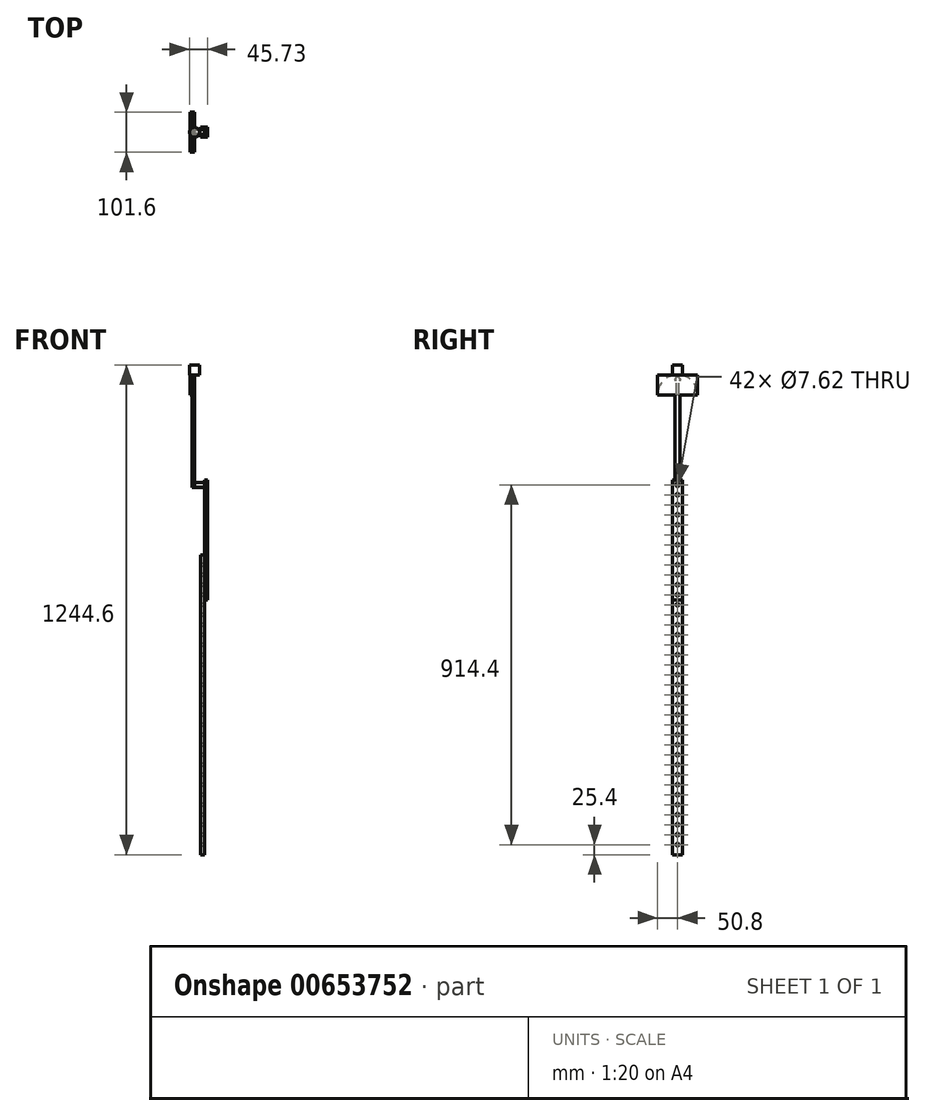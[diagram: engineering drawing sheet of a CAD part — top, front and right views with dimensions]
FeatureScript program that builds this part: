
annotation { "Feature Type Name" : "Feature", "Feature Type Description" : "" }
export const myFeature = defineFeature(function(context is Context, id is Id, definition is map)
    precondition{}
    {
        {
            var Q0;
            Q0=qCreatedBy(makeId("Right.planeOp"),FACE);
            var sketch = newSketch(context, id + "F0", { "sketchPlane" : qUnion([Q0])});
            skLineSegment(sketch, "E0.bottom", {"start": v(0, 762) * mm, "end": v(25.4, 762) * mm});
            skLineSegment(sketch, "E0.top", {"start": v(0, 0) * mm, "end": v(25.4, 0) * mm});
            skLineSegment(sketch, "E0.left", {"start": v(0, 762) * mm, "end": v(0, 0) * mm});
            skLineSegment(sketch, "E0.right", {"start": v(25.4, 762) * mm, "end": v(25.4, 0) * mm});
            skCircle(sketch, "E1", {"center": v(12.7, 25.4) * mm, "radius": 3.81 * mm});
            skCircle(sketch, "E2.0.1.0", {"center": v(12.7, 50.8) * mm, "radius": 3.81 * mm});
            skCircle(sketch, "E2.0.2.0", {"center": v(12.7, 76.2) * mm, "radius": 3.81 * mm});
            skCircle(sketch, "E2.0.3.0", {"center": v(12.7, 101.6) * mm, "radius": 3.81 * mm});
            skCircle(sketch, "E2.0.4.0", {"center": v(12.7, 127) * mm, "radius": 3.81 * mm});
            skCircle(sketch, "E2.0.5.0", {"center": v(12.7, 152.4) * mm, "radius": 3.81 * mm});
            skCircle(sketch, "E2.0.6.0", {"center": v(12.7, 177.8) * mm, "radius": 3.81 * mm});
            skCircle(sketch, "E2.0.7.0", {"center": v(12.7, 203.2) * mm, "radius": 3.81 * mm});
            skCircle(sketch, "E2.0.8.0", {"center": v(12.7, 228.6) * mm, "radius": 3.81 * mm});
            skCircle(sketch, "E2.0.9.0", {"center": v(12.7, 254) * mm, "radius": 3.81 * mm});
            skCircle(sketch, "E2.0.10.0", {"center": v(12.7, 279.4) * mm, "radius": 3.81 * mm});
            skCircle(sketch, "E2.0.11.0", {"center": v(12.7, 304.8) * mm, "radius": 3.81 * mm});
            skCircle(sketch, "E2.0.12.0", {"center": v(12.7, 330.2) * mm, "radius": 3.81 * mm});
            skCircle(sketch, "E2.0.13.0", {"center": v(12.7, 355.6) * mm, "radius": 3.81 * mm});
            skCircle(sketch, "E2.0.14.0", {"center": v(12.7, 381) * mm, "radius": 3.81 * mm});
            skCircle(sketch, "E2.0.15.0", {"center": v(12.7, 406.4) * mm, "radius": 3.81 * mm});
            skCircle(sketch, "E2.0.16.0", {"center": v(12.7, 431.8) * mm, "radius": 3.81 * mm});
            skCircle(sketch, "E2.0.17.0", {"center": v(12.7, 457.2) * mm, "radius": 3.81 * mm});
            skCircle(sketch, "E2.0.18.0", {"center": v(12.7, 482.6) * mm, "radius": 3.81 * mm});
            skCircle(sketch, "E2.0.19.0", {"center": v(12.7, 508) * mm, "radius": 3.81 * mm});
            skCircle(sketch, "E2.0.20.0", {"center": v(12.7, 533.4) * mm, "radius": 3.81 * mm});
            skCircle(sketch, "E2.0.21.0", {"center": v(12.7, 558.8) * mm, "radius": 3.81 * mm});
            skCircle(sketch, "E2.0.22.0", {"center": v(12.7, 584.2) * mm, "radius": 3.81 * mm});
            skCircle(sketch, "E2.0.23.0", {"center": v(12.7, 609.6) * mm, "radius": 3.81 * mm});
            skCircle(sketch, "E2.0.24.0", {"center": v(12.7, 635) * mm, "radius": 3.81 * mm});
            skCircle(sketch, "E2.0.25.0", {"center": v(12.7, 660.4) * mm, "radius": 3.81 * mm});
            skCircle(sketch, "E2.0.26.0", {"center": v(12.7, 685.8) * mm, "radius": 3.81 * mm});
            skCircle(sketch, "E2.0.27.0", {"center": v(12.7, 711.2) * mm, "radius": 3.81 * mm});
            skCircle(sketch, "E2.0.28.0", {"center": v(12.7, 736.6) * mm, "radius": 3.81 * mm});
            skLineSegment(sketch, "E2.direction1", {"start": v(12.7, 25.4) * mm, "end": v(38.1, 25.4) * mm, "construction": true});
            skLineSegment(sketch, "E2.direction2", {"start": v(12.7, 25.4) * mm, "end": v(12.7, 50.8) * mm, "construction": true});
            skSolve(sketch);
        }
        {
            var Q0;
            Q0=makeQuery(id+"F0.imprint","IMPRINT",FACE,{"disambiguationData":[TD([[makeQuery(id+"F0.imprint","IMPRINT",EDGE,{"derivedFrom":sQuery(id+"F0.wireOp",EDGE,"E0.bottom")}),-1.0]])]});
            extrude(context, id + "F1", {"entities" : qUnion([Q0]), "depth" : 9.52 * mm, "offsetDistance" : 25.4 * mm});
        }
        {
            var Q0;
            Q0=makeQuery(id+"F1.opExtrude","CAP_FACE",FACE,{"disambiguationData":[OSD([sQuery(id+"F0.wireOp",EDGE,"E0.bottom"),sQuery(id+"F0.wireOp",EDGE,"E0.top"),sQuery(id+"F0.wireOp",EDGE,"E0.left"),sQuery(id+"F0.wireOp",EDGE,"E0.right"),sQuery(id+"F0.wireOp",EDGE,"E1"),sQuery(id+"F0.wireOp",EDGE,"E2.0.1.0"),sQuery(id+"F0.wireOp",EDGE,"E2.0.2.0"),sQuery(id+"F0.wireOp",EDGE,"E2.0.3.0"),sQuery(id+"F0.wireOp",EDGE,"E2.0.4.0"),sQuery(id+"F0.wireOp",EDGE,"E2.0.5.0"),sQuery(id+"F0.wireOp",EDGE,"E2.0.6.0"),sQuery(id+"F0.wireOp",EDGE,"E2.0.7.0"),sQuery(id+"F0.wireOp",EDGE,"E2.0.8.0"),sQuery(id+"F0.wireOp",EDGE,"E2.0.9.0"),sQuery(id+"F0.wireOp",EDGE,"E2.0.10.0"),sQuery(id+"F0.wireOp",EDGE,"E2.0.11.0"),sQuery(id+"F0.wireOp",EDGE,"E2.0.12.0"),sQuery(id+"F0.wireOp",EDGE,"E2.0.13.0"),sQuery(id+"F0.wireOp",EDGE,"E2.0.14.0"),sQuery(id+"F0.wireOp",EDGE,"E2.0.15.0"),sQuery(id+"F0.wireOp",EDGE,"E2.0.16.0"),sQuery(id+"F0.wireOp",EDGE,"E2.0.17.0"),sQuery(id+"F0.wireOp",EDGE,"E2.0.18.0"),sQuery(id+"F0.wireOp",EDGE,"E2.0.19.0"),sQuery(id+"F0.wireOp",EDGE,"E2.0.20.0"),sQuery(id+"F0.wireOp",EDGE,"E2.0.21.0"),sQuery(id+"F0.wireOp",EDGE,"E2.0.22.0"),sQuery(id+"F0.wireOp",EDGE,"E2.0.23.0"),sQuery(id+"F0.wireOp",EDGE,"E2.0.24.0"),sQuery(id+"F0.wireOp",EDGE,"E2.0.25.0"),sQuery(id+"F0.wireOp",EDGE,"E2.0.26.0"),sQuery(id+"F0.wireOp",EDGE,"E2.0.27.0"),sQuery(id+"F0.wireOp",EDGE,"E2.0.28.0")])],"isStart":false});
            var sketch = newSketch(context, id + "F2", { "sketchPlane" : qUnion([Q0])});
            skLineSegment(sketch, "E3.bottom", {"start": v(0, 952.5) * mm, "end": v(25.4, 952.5) * mm});
            skLineSegment(sketch, "E3.top", {"start": v(0, 647.7) * mm, "end": v(25.4, 647.7) * mm});
            skLineSegment(sketch, "E3.left", {"start": v(0, 952.5) * mm, "end": v(0, 647.7) * mm});
            skLineSegment(sketch, "E3.right", {"start": v(25.4, 952.5) * mm, "end": v(25.4, 647.7) * mm});
            skPoint(sketch, "E4", {"position": v(12.7, 25.4) * mm});
            skCircle(sketch, "E5", {"center": v(12.7, 660.4) * mm, "radius": 3.81 * mm});
            skCircle(sketch, "E6.0.1.0", {"center": v(12.7, 685.8) * mm, "radius": 3.81 * mm});
            skCircle(sketch, "E6.0.2.0", {"center": v(12.7, 711.2) * mm, "radius": 3.81 * mm});
            skCircle(sketch, "E6.0.3.0", {"center": v(12.7, 736.6) * mm, "radius": 3.81 * mm});
            skCircle(sketch, "E6.0.4.0", {"center": v(12.7, 762) * mm, "radius": 3.81 * mm});
            skCircle(sketch, "E6.0.5.0", {"center": v(12.7, 787.4) * mm, "radius": 3.81 * mm});
            skCircle(sketch, "E6.0.6.0", {"center": v(12.7, 812.8) * mm, "radius": 3.81 * mm});
            skCircle(sketch, "E6.0.7.0", {"center": v(12.7, 838.2) * mm, "radius": 3.81 * mm});
            skCircle(sketch, "E6.0.8.0", {"center": v(12.7, 863.6) * mm, "radius": 3.81 * mm});
            skCircle(sketch, "E6.0.9.0", {"center": v(12.7, 889) * mm, "radius": 3.81 * mm});
            skCircle(sketch, "E6.0.10.0", {"center": v(12.7, 914.4) * mm, "radius": 3.81 * mm});
            skCircle(sketch, "E6.0.11.0", {"center": v(12.7, 939.8) * mm, "radius": 3.81 * mm});
            skLineSegment(sketch, "E6.direction1", {"start": v(12.7, 660.4) * mm, "end": v(38.1, 660.4) * mm, "construction": true});
            skLineSegment(sketch, "E6.direction2", {"start": v(12.7, 660.4) * mm, "end": v(12.7, 685.8) * mm, "construction": true});
            skSolve(sketch);
        }
        {
            var Q0;
            {var subQ0=sQuery(id+"F2.wireOp",EDGE,"E3.bottom");Q0=makeQuery(id+"F2.imprint","IMPRINT",FACE,{"disambiguationData":[TD([[makeQuery(id+"F2.imprint","IMPRINT",EDGE,{"derivedFrom":subQ0}),-1.0]])]});}
            var Q1;
            {var subQ3=sQuery(id+"F2.wireOp",EDGE,"E3.top");Q1=makeQuery(id+"F2.imprint","IMPRINT",FACE,{"disambiguationData":[TD([[makeQuery(id+"F2.imprint","IMPRINT",EDGE,{"derivedFrom":subQ3}),1.0]])]});}
            extrude(context, id + "F3", {"entities" : qUnion([Q0, Q1]), "depth" : 7.62 * mm, "offsetDistance" : 25.4 * mm});
        }
        {
            var Q0;
            Q0=makeQuery(id+"F3.opExtrude","CAP_FACE",FACE,{"disambiguationData":[OSD([sQuery(id+"F2.wireOp",EDGE,"E3.bottom"),sQuery(id+"F2.wireOp",EDGE,"E3.top"),sQuery(id+"F2.wireOp",EDGE,"E3.left"),sQuery(id+"F2.wireOp",EDGE,"E3.right"),sQuery(id+"F2.wireOp",EDGE,"E5"),sQuery(id+"F2.wireOp",EDGE,"E6.0.1.0"),sQuery(id+"F2.wireOp",EDGE,"E6.0.2.0"),sQuery(id+"F2.wireOp",EDGE,"E6.0.3.0"),sQuery(id+"F2.wireOp",EDGE,"E6.0.4.0"),sQuery(id+"F2.wireOp",EDGE,"E6.0.5.0"),sQuery(id+"F2.wireOp",EDGE,"E6.0.6.0"),sQuery(id+"F2.wireOp",EDGE,"E6.0.7.0"),sQuery(id+"F2.wireOp",EDGE,"E6.0.8.0"),sQuery(id+"F2.wireOp",EDGE,"E6.0.9.0"),sQuery(id+"F2.wireOp",EDGE,"E6.0.10.0"),sQuery(id+"F2.wireOp",EDGE,"E6.0.11.0")])],"isStart":true});
            var sketch = newSketch(context, id + "F4", { "sketchPlane" : qUnion([Q0])});
            skCircle(sketch, "E7", {"center": v(-12.7, 939.8) * mm, "radius": 6.35 * mm});
            skSolve(sketch);
        }
        {
            var Q0;
            Q0=makeQuery(id+"F4.imprint","IMPRINT",FACE,{"disambiguationData":[TD([[makeQuery(id+"F4.imprint","IMPRINT",EDGE,{"derivedFrom":sQuery(id+"F4.wireOp",EDGE,"E7")}),1.0]])]});
            extrude(context, id + "F5", {"entities" : qUnion([Q0]), "operationType" : NewBodyOperationType.ADD, "depth" : 25.4 * mm, "offsetDistance" : 25.4 * mm});
        }
        {
            var Q0;
            Q0=makeQuery(id+"F5.opExtrude","CAP_FACE",FACE,{"disambiguationData":[OSD([sQuery(id+"F2.wireOp",EDGE,"E6.0.11.0"),sQuery(id+"F4.wireOp",EDGE,"E7")])],"isStart":false});
            var sketch = newSketch(context, id + "F6", { "sketchPlane" : qUnion([Q0])});
            skLineSegment(sketch, "E8.bottom", {"start": v(-19.05, 1193.8) * mm, "end": v(-6.35, 1193.8) * mm});
            skLineSegment(sketch, "E8.top", {"start": v(-19.05, 933.45) * mm, "end": v(-6.35, 933.45) * mm});
            skLineSegment(sketch, "E8.left", {"start": v(-19.05, 1193.8) * mm, "end": v(-19.05, 933.45) * mm});
            skLineSegment(sketch, "E8.right", {"start": v(-6.35, 1193.8) * mm, "end": v(-6.35, 933.45) * mm});
            skPoint(sketch, "E9", {"position": v(-12.7, 939.8) * mm});
            skLineSegment(sketch, "E10.bottom", {"start": v(-63.5, 1168.4) * mm, "end": v(38.1, 1168.4) * mm});
            skLineSegment(sketch, "E10.top", {"start": v(-63.5, 1219.2) * mm, "end": v(38.1, 1219.2) * mm});
            skLineSegment(sketch, "E10.left", {"start": v(-63.5, 1168.4) * mm, "end": v(-63.5, 1219.2) * mm});
            skLineSegment(sketch, "E10.right", {"start": v(38.1, 1168.4) * mm, "end": v(38.1, 1219.2) * mm});
            skSolve(sketch);
        }
        {
            var Q0;
            Q0=makeQuery(id+"F6.imprint","IMPRINT",FACE,{"disambiguationData":[TD([[makeQuery(id+"F6.imprint","IMPRINT",EDGE,{"derivedFrom":makeQuery(id+"F5.opExtrude","CAP_EDGE",EDGE,{"disambiguationData":[OSD([sQuery(id+"F2.wireOp",EDGE,"E6.0.11.0")])],"isStart":false})}),1.0]])]});
            var Q1;
            {var subQ5=sQuery(id+"F6.wireOp",EDGE,"E8.bottom");Q1=makeQuery(id+"F6.imprint","IMPRINT",FACE,{"disambiguationData":[TD([[makeQuery(id+"F6.imprint","IMPRINT",EDGE,{"derivedFrom":subQ5}),1.0]])]});}
            var Q2;
            {var subQ0=sQuery(id+"F6.wireOp",EDGE,"E8.bottom");Q2=makeQuery(id+"F6.imprint","IMPRINT",FACE,{"disambiguationData":[TD([[makeQuery(id+"F6.imprint","IMPRINT",EDGE,{"derivedFrom":subQ0}),-1.0]])]});}
            var Q3;
            {var subQ0=sQuery(id+"F6.wireOp",EDGE,"E10.bottom");var subQ1=sQuery(id+"F6.wireOp",EDGE,"E8.left");var subQ2=makeQuery(id+"F6.imprint","INTERSECT",VERTEX,{"derivedFrom":[subQ1,subQ0]});Q3=makeQuery(id+"F6.imprint","IMPRINT",FACE,{"disambiguationData":[TD([[makeQuery(id+"F6.imprint","IMPRINT",EDGE,{"disambiguationData":[TD([[subQ2,-1.0]])],"derivedFrom":subQ1}),1.0]])]});}
            extrude(context, id + "F7", {"entities" : qUnion([Q0, Q1, Q2, Q3]), "depth" : 6.35 * mm, "offsetDistance" : 25.4 * mm});
        }
        {
            var Q0;
            Q0=makeQuery(id+"F7.opExtrude","CAP_FACE",FACE,{"disambiguationData":[OSD([sQuery(id+"F2.wireOp",EDGE,"E6.0.11.0"),sQuery(id+"F4.wireOp",EDGE,"E7"),sQuery(id+"F6.wireOp",EDGE,"E8.left"),sQuery(id+"F6.wireOp",EDGE,"E8.right"),sQuery(id+"F6.wireOp",EDGE,"E10.bottom"),sQuery(id+"F6.wireOp",EDGE,"E10.top"),sQuery(id+"F6.wireOp",EDGE,"E10.left"),sQuery(id+"F6.wireOp",EDGE,"E10.right")])],"isStart":false});
            var sketch = newSketch(context, id + "F8", { "sketchPlane" : qUnion([Q0])});
            skCircle(sketch, "E11", {"center": v(-12.7, 1168.4) * mm, "radius": 50.8 * mm});
            skPoint(sketch, "E11.centerSnap0", {"position": v(-12.7, 1219.2) * mm});
            skLineSegment(sketch, "E12.bottom", {"start": v(-15.88, 1168.4) * mm, "end": v(-9.53, 1168.4) * mm});
            skLineSegment(sketch, "E12.top", {"start": v(-15.88, 1206.5) * mm, "end": v(-9.53, 1206.5) * mm});
            skLineSegment(sketch, "E12.left", {"start": v(-15.88, 1168.4) * mm, "end": v(-15.88, 1206.5) * mm});
            skLineSegment(sketch, "E12.right", {"start": v(-9.53, 1168.4) * mm, "end": v(-9.53, 1206.5) * mm});
            skLineSegment(sketch, "E13", {"start": v(-15.88, 1206.5) * mm, "end": v(-21.04, 1206.5) * mm});
            skLineSegment(sketch, "E14", {"start": v(-21.04, 1206.5) * mm, "end": v(-12.7, 1219.2) * mm});
            skPoint(sketch, "E14.endSnap0", {"position": v(-12.7, 1206.5) * mm});
            skLineSegment(sketch, "E15", {"start": v(-12.7, 1219.2) * mm, "end": v(-4.36, 1206.5) * mm});
            skLineSegment(sketch, "E16", {"start": v(-4.36, 1206.5) * mm, "end": v(-9.53, 1206.5) * mm});
            skSolve(sketch);
        }
        {
            var Q0;
            Q0=makeQuery(id+"F8.imprint","IMPRINT",FACE,{"disambiguationData":[TD([[makeQuery(id+"F8.imprint","IMPRINT",EDGE,{"derivedFrom":sQuery(id+"F8.wireOp",EDGE,"E12.top")}),1.0]])]});
            var Q1;
            Q1=makeQuery(id+"F8.imprint","IMPRINT",FACE,{"disambiguationData":[TD([[makeQuery(id+"F8.imprint","IMPRINT",EDGE,{"derivedFrom":sQuery(id+"F8.wireOp",EDGE,"E12.bottom")}),1.0]])]});
            var Q2;
            {var subQ1=sQuery(id+"F6.wireOp",EDGE,"E10.left");var subQ2=makeQuery(id+"F7.opExtrude","CAP_EDGE",EDGE,{"disambiguationData":[OSD([subQ1])],"isStart":false});Q2=makeQuery(id+"F8.imprint","IMPRINT",FACE,{"disambiguationData":[TD([[makeQuery(id+"F8.imprint","IMPRINT",EDGE,{"derivedFrom":subQ2}),-1.0]])]});}
            var Q3;
            {var subQ1=sQuery(id+"F6.wireOp",EDGE,"E10.right");var subQ2=makeQuery(id+"F7.opExtrude","CAP_EDGE",EDGE,{"disambiguationData":[OSD([subQ1])],"isStart":false});Q3=makeQuery(id+"F8.imprint","IMPRINT",FACE,{"disambiguationData":[TD([[makeQuery(id+"F8.imprint","IMPRINT",EDGE,{"derivedFrom":subQ2}),1.0]])]});}
            extrude(context, id + "F9", {"entities" : qUnion([Q0, Q1, Q2, Q3]), "depth" : 5.08 * mm, "offsetDistance" : 25.4 * mm});
        }
        {
            var Q0;
            Q0=makeQuery(id+"F7.opExtrude","SWEPT_FACE",FACE,{"disambiguationData":[OSD([sQuery(id+"F6.wireOp",EDGE,"E10.top")])]});
            var sketch = newSketch(context, id + "F10", { "sketchPlane" : qUnion([Q0])});
            skCircle(sketch, "E17", {"center": v(-15.88, 12.7) * mm, "radius": 12.7 * mm});
            skSolve(sketch);
        }
        {
            var Q0;
            {var subQ0=sQuery(id+"F10.wireOp",EDGE,"E17");var subQ1=makeQuery(id+"F7.opExtrude","CAP_EDGE",EDGE,{"disambiguationData":[OSD([sQuery(id+"F6.wireOp",EDGE,"E10.top")])],"isStart":true});var subQ2=makeQuery(id+"F10.imprint","INTERSECT",VERTEX,{"disambiguationData":[OD(0.0)],"derivedFrom":[subQ1,subQ0]});Q0=makeQuery(id+"F10.imprint","IMPRINT",FACE,{"disambiguationData":[TD([[makeQuery(id+"F10.imprint","IMPRINT",EDGE,{"disambiguationData":[TD([[subQ2,1.0]])],"derivedFrom":subQ0}),1.0]])]});}
            var Q1;
            {var subQ0=sQuery(id+"F10.wireOp",EDGE,"E17");var subQ1=sQuery(id+"F6.wireOp",EDGE,"E10.top");var subQ2=makeQuery(id+"F7.opExtrude","CAP_EDGE",EDGE,{"disambiguationData":[OSD([subQ1])],"isStart":false});var subQ3=makeQuery(id+"F10.imprint","INTERSECT",VERTEX,{"disambiguationData":[OD(0.0)],"derivedFrom":[subQ2,subQ0]});Q1=makeQuery(id+"F10.imprint","IMPRINT",FACE,{"disambiguationData":[TD([[makeQuery(id+"F10.imprint","IMPRINT",EDGE,{"disambiguationData":[TD([[subQ3,1.0]])],"derivedFrom":subQ0}),1.0]])]});}
            var Q2;
            {var subQ0=sQuery(id+"F10.wireOp",EDGE,"E17");var subQ1=makeQuery(id+"F7.opExtrude","CAP_EDGE",EDGE,{"disambiguationData":[OSD([sQuery(id+"F6.wireOp",EDGE,"E10.top")])],"isStart":false});var subQ2=makeQuery(id+"F10.imprint","INTERSECT",VERTEX,{"disambiguationData":[OD(0.0)],"derivedFrom":[subQ1,subQ0]});Q2=makeQuery(id+"F10.imprint","IMPRINT",FACE,{"disambiguationData":[TD([[makeQuery(id+"F10.imprint","IMPRINT",EDGE,{"disambiguationData":[TD([[subQ2,-1.0]])],"derivedFrom":subQ0}),1.0]])]});}
            extrude(context, id + "F11", {"entities" : qUnion([Q0, Q1, Q2]), "depth" : 25.4 * mm, "offsetDistance" : 25.4 * mm});
        }
    });
